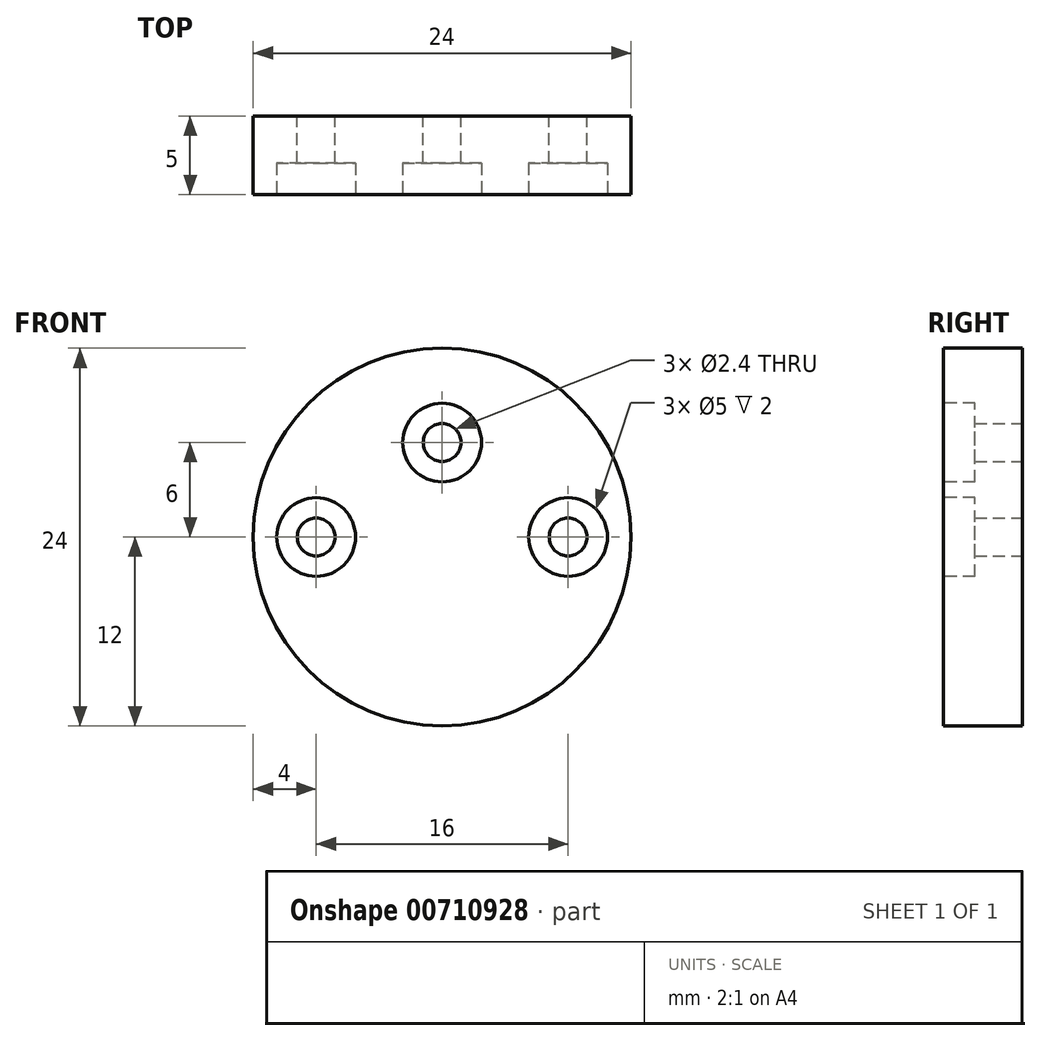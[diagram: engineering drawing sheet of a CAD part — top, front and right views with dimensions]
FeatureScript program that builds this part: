
annotation { "Feature Type Name" : "Feature", "Feature Type Description" : "" }
export const myFeature = defineFeature(function(context is Context, id is Id, definition is map)
    precondition{}
    {
        {
            var Q0;
            Q0=qCreatedBy(makeId("Front.planeOp"),FACE);
            var sketch = newSketch(context, id + "F0", { "sketchPlane" : qUnion([Q0])});
            skCircle(sketch, "E0", {"center": v(0, 0) * mm, "radius": 12 * mm});
            skSolve(sketch);
        }
        {
            var Q0;
            Q0 = qSketchRegion(id + "F0", true);
            var Q1;
            Q1=sQuery(id+"F0.wireOp",EDGE,"E0");
            extrude(context, id + "F1", {"entities" : qUnion([Q0]), "surfaceOperationType" : NewSurfaceOperationType.ADD, "surfaceEntities" : qUnion([Q1]), "depth" : 5 * mm, "offsetDistance" : 25 * mm});
        }
        {
            var Q0;
            Q0=makeQuery(id+"F1.opExtrude","CAP_FACE",FACE,{"disambiguationData":[OSD([sQuery(id+"F0.wireOp",EDGE,"E0")])],"isStart":true});
            var sketch = newSketch(context, id + "F2", { "sketchPlane" : qUnion([Q0])});
            skCircle(sketch, "E1", {"center": v(8, 0) * mm, "radius": 1.2 * mm});
            skLineSegment(sketch, "E2", {"start": v(0, 12) * mm, "end": v(0, -12) * mm, "construction": true});
            skCircle(sketch, "E3.MirrorC", {"center": v(-8, 0) * mm, "radius": 1.2 * mm});
            skCircle(sketch, "E4", {"center": v(0, 6) * mm, "radius": 1.2 * mm});
            skSolve(sketch);
        }
        {
            var Q0;
            Q0 = qSketchRegion(id + "F2", true);
            extrude(context, id + "F3", {"entities" : qUnion([Q0]), "operationType" : NewBodyOperationType.REMOVE, "oppositeDirection" : true, "depth" : 5 * mm, "offsetDistance" : 25 * mm});
        }
        {
            var Q0;
            Q0=makeQuery(id+"F1.opExtrude","CAP_FACE",FACE,{"disambiguationData":[OSD([sQuery(id+"F0.wireOp",EDGE,"E0")])],"isStart":false});
            var sketch = newSketch(context, id + "F4", { "sketchPlane" : qUnion([Q0])});
            skCircle(sketch, "E5", {"center": v(0, 6) * mm, "radius": 2.5 * mm});
            skCircle(sketch, "E6", {"center": v(8, 0) * mm, "radius": 2.5 * mm});
            skCircle(sketch, "E7", {"center": v(-8, 0) * mm, "radius": 2.5 * mm});
            skSolve(sketch);
        }
        {
            var Q0;
            Q0 = qSketchRegion(id + "F4", true);
            extrude(context, id + "F5", {"entities" : qUnion([Q0]), "operationType" : NewBodyOperationType.REMOVE, "oppositeDirection" : true, "depth" : 2 * mm, "offsetDistance" : 25 * mm});
        }
    });
